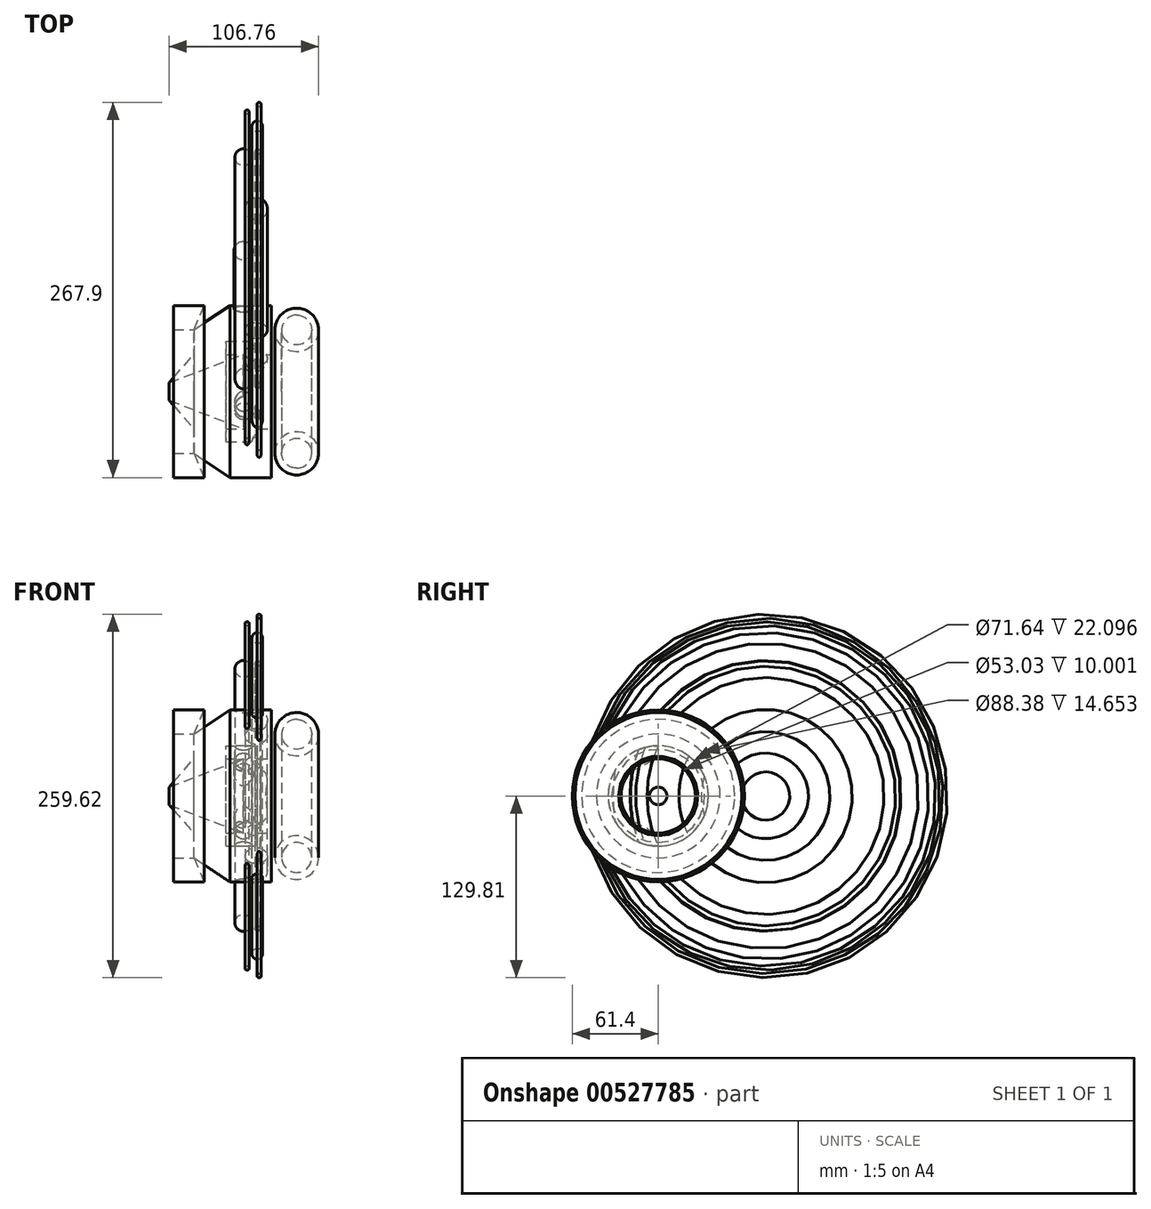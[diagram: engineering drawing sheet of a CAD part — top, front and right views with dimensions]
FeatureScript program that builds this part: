
annotation { "Feature Type Name" : "Feature", "Feature Type Description" : "" }
export const myFeature = defineFeature(function(context is Context, id is Id, definition is map)
    precondition{}
    {
        {
            var Q0;
            Q0=qCreatedBy(makeId("Front.planeOp"),FACE);
            var sketch = newSketch(context, id + "F0", { "sketchPlane" : qUnion([Q0])});
            skLineSegment(sketch, "E0", {"start": v(0, 0) * mm, "end": v(-102.1, 0) * mm});
            skLineSegment(sketch, "E1", {"start": v(0, 26.51) * mm, "end": v(-10, 26.51) * mm});
            skLineSegment(sketch, "E2", {"start": v(-55.12, 26.51) * mm, "end": v(-55.12, 44.2) * mm});
            skLineSegment(sketch, "E3", {"start": v(-55.12, 44.2) * mm, "end": v(-69.78, 44.2) * mm});
            skLineSegment(sketch, "E4", {"start": v(-69.78, 44.2) * mm, "end": v(-69.78, 61.4) * mm});
            skLineSegment(sketch, "E5", {"start": v(-69.78, 61.4) * mm, "end": v(-47.68, 61.4) * mm});
            skLineSegment(sketch, "E6", {"start": v(0, 61.4) * mm, "end": v(0, 26.51) * mm});
            skLineSegment(sketch, "E7", {"start": v(-32.1, 26.51) * mm, "end": v(-32.1, 35.82) * mm});
            skLineSegment(sketch, "E8", {"start": v(-32.1, 35.82) * mm, "end": v(-10, 35.82) * mm});
            skLineSegment(sketch, "E9", {"start": v(-10, 35.82) * mm, "end": v(-10, 26.51) * mm});
            skLineSegment(sketch, "E10", {"start": v(-55.12, 44.2) * mm, "end": v(-47.68, 61.4) * mm});
            skLineSegment(sketch, "E11", {"start": v(-55.12, 44.2) * mm, "end": v(-29.54, 61.4) * mm});
            skLineSegment(sketch, "E12.trimOffspring", {"start": v(-32.1, 26.51) * mm, "end": v(-55.12, 26.51) * mm});
            skLineSegment(sketch, "E13.trimOffspring", {"start": v(-29.54, 61.4) * mm, "end": v(0, 61.4) * mm});
            skLineSegment(sketch, "E14", {"start": v(-55.12, 26.51) * mm, "end": v(-72.96, 6.28) * mm});
            skLineSegment(sketch, "E15", {"start": v(-72.96, 6.28) * mm, "end": v(-19.93, 26.51) * mm});
            skLineSegment(sketch, "E16", {"start": v(-19.93, 26.51) * mm, "end": v(-32.1, 26.51) * mm});
            skCircle(sketch, "E17", {"center": v(18.21, 43.96) * mm, "radius": 15.59 * mm});
            skPoint(sketch, "E17.centerSnap0", {"position": v(0, 43.96) * mm});
            skCircle(sketch, "E18", {"center": v(18.21, 43.96) * mm, "radius": 10.7 * mm});
            skSolve(sketch);
        }
        {
            var Q0;
            Q0=makeQuery(id+"F0.imprint","IMPRINT",FACE,{"disambiguationData":[TD([[makeQuery(id+"F0.imprint","IMPRINT",EDGE,{"derivedFrom":sQuery(id+"F0.wireOp",EDGE,"E1")}),-1.0]])]});
            var Q1;
            Q1=makeQuery(id+"F0.imprint","IMPRINT",FACE,{"disambiguationData":[TD([[makeQuery(id+"F0.imprint","IMPRINT",EDGE,{"derivedFrom":sQuery(id+"F0.wireOp",EDGE,"E3")}),-1.0]])]});
            var Q2;
            Q2=makeQuery(id+"F0.imprint","IMPRINT",FACE,{"disambiguationData":[TD([[makeQuery(id+"F0.imprint","IMPRINT",EDGE,{"derivedFrom":sQuery(id+"F0.wireOp",EDGE,"E12.trimOffspring")}),1.0]])]});
            var Q3;
            Q3=makeQuery(id+"F0.imprint","IMPRINT",FACE,{"disambiguationData":[TD([[makeQuery(id+"F0.imprint","IMPRINT",EDGE,{"derivedFrom":sQuery(id+"F0.wireOp",EDGE,"E17")}),1.0]])]});
            var Q4;
            Q4=sQuery(id+"F0.wireOp",EDGE,"E0");
            revolve(context, id + "F1", {"entities" : qUnion([Q0, Q1, Q2, Q3]), "axis" : qUnion([Q4]), "revolveType" : RevolveType.FULL});
        }
        {
            var Q0;
            Q0=qCreatedBy(makeId("Top.planeOp"),FACE);
            var sketch = newSketch(context, id + "F2", { "sketchPlane" : qUnion([Q0])});
            skCircle(sketch, "E19", {"center": v(-19.77, 52.8) * mm, "radius": 6.7 * mm});
            skCircle(sketch, "E20", {"center": v(-10.7, 22.8) * mm, "radius": 7.96 * mm});
            skCircle(sketch, "E21", {"center": v(-19.77, -13.96) * mm, "radius": 6.09 * mm});
            skCircle(sketch, "E22", {"center": v(-10, -36.05) * mm, "radius": 3.79 * mm});
            skCircle(sketch, "E23", {"center": v(-17.21, -46.28) * mm, "radius": 1.47 * mm});
            skCircle(sketch, "E24", {"center": v(-9.77, -17.9) * mm, "radius": 1.88 * mm});
            skCircle(sketch, "E25", {"center": v(-8.6, -51.63) * mm, "radius": 1.49 * mm});
            skLineSegment(sketch, "E26", {"start": v(0, 76.69) * mm, "end": v(-42.65, 76.69) * mm});
            skSolve(sketch);
        }
        {
            var Q0;
            Q0 = qSketchRegion(id + "F2", true);
            var Q1;
            Q1=sQuery(id+"F2.wireOp",EDGE,"E26");
            revolve(context, id + "F3", {"operationType" : NewBodyOperationType.ADD, "entities" : qUnion([Q0]), "axis" : qUnion([Q1]), "revolveType" : RevolveType.FULL});
        }
    });
